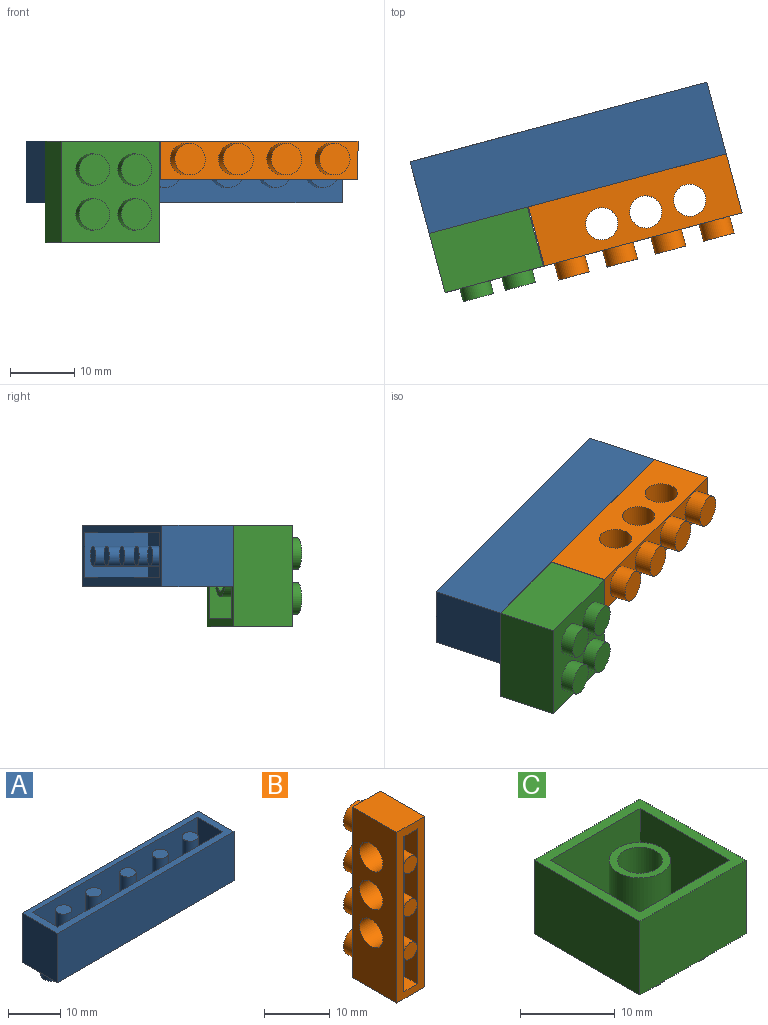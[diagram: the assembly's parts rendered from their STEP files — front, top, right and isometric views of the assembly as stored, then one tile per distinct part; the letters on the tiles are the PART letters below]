
ASSEMBLY  parts=3 mates=3
PART A: 33 faces, bbox 47.7x9.6x13.7 mm
  f0: plane 47.7x9.6mm, normal (0,0,1), area 150.9mm2, adj f1,f2,f3,f4,f18,f19,f20,f21
  f1: plane 11.5x9.6mm, normal (1,0,0), area 110.4mm2, adj f0,f2,f4,f5
  f2: plane 47.7x11.5mm, normal (0,1,0), area 548.5mm2, adj f0,f1,f3,f5
  f3: plane 11.5x9.6mm, normal (-1,0,0), area 110.4mm2, adj f0,f2,f4,f5
  f4: plane 47.7x11.5mm, normal (0,-1,0), area 548.5mm2, adj f0,f1,f3,f5
  f5: plane 47.7x9.6mm, normal (0,0,-1), area 349.3mm2, adj f1,f2,f3,f4,f6,f8,f10,f12
  f6: cylinder r=2.4mm len=4.8mm, axis (0,0,1), area 33.2mm2, adj f5,f7
  f7: plane 4.8x4.8mm, normal (0,0,-1), area 18.1mm2, adj f6
  f8: cylinder r=2.4mm len=4.8mm, axis (0,0,1), area 33.2mm2, adj f5,f9
  f9: plane 4.8x4.8mm, normal (0,0,-1), area 18.1mm2, adj f8
  f10: cylinder r=2.4mm len=4.8mm, axis (0,0,1), area 33.2mm2, adj f5,f11
  f11: plane 4.8x4.8mm, normal (0,0,-1), area 18.1mm2, adj f10
  f12: cylinder r=2.4mm len=4.8mm, axis (0,0,1), area 33.2mm2, adj f5,f13
  f13: plane 4.8x4.8mm, normal (0,0,-1), area 18.1mm2, adj f12
  f14: cylinder r=2.4mm len=4.8mm, axis (0,0,1), area 33.2mm2, adj f5,f15
  f15: plane 4.8x4.8mm, normal (0,0,-1), area 18.1mm2, adj f14
  f16: cylinder r=2.4mm len=4.8mm, axis (0,0,1), area 33.2mm2, adj f5,f17
  f17: plane 4.8x4.8mm, normal (0,0,-1), area 18.1mm2, adj f16
  f18: plane 44.54x10.15mm, normal (0,-1,0), area 452.1mm2, adj f0,f19,f21,f22
  f19: plane 10.15x6.89mm, normal (1,0,0), area 70mm2, adj f0,f18,f20,f22
  f20: plane 44.54x10.15mm, normal (0,1,0), area 452.1mm2, adj f0,f19,f21,f22
  f21: plane 10.15x6.89mm, normal (-1,0,0), area 70mm2, adj f0,f18,f20,f22
  f22: plane 44.54x6.89mm, normal (0,0,1), area 269.3mm2, adj f18,f19,f20,f21,f23,f25,f27,f29
  f23: cylinder r=1.55mm len=10.15mm, axis (0,0,-1), area 98.9mm2, adj f22,f24
  f24: plane 3.1x3.1mm, normal (0,0,1), area 7.5mm2, adj f23
  f25: cylinder r=1.55mm len=10.15mm, axis (0,0,-1), area 98.9mm2, adj f22,f26
  f26: plane 3.1x3.1mm, normal (0,0,1), area 7.5mm2, adj f25
  f27: cylinder r=1.55mm len=10.15mm, axis (0,0,-1), area 98.9mm2, adj f22,f28
  f28: plane 3.1x3.1mm, normal (0,0,1), area 7.5mm2, adj f27
  f29: cylinder r=1.55mm len=10.15mm, axis (0,0,-1), area 98.9mm2, adj f22,f30
  f30: plane 3.1x3.1mm, normal (0,0,1), area 7.5mm2, adj f29
  f31: cylinder r=1.55mm len=10.15mm, axis (0,0,-1), area 98.9mm2, adj f22,f32
  f32: plane 3.1x3.1mm, normal (0,0,1), area 7.5mm2, adj f31
PART B: 28 faces, bbox 6x12.2x31.8 mm
  f0: plane 28.9x2.78mm, normal (1,0,0), area 70.3mm2, adj f1,f6,f19,f21,f22,f23,f24,f25
  f1: plane 28.9x2.92mm, normal (0,-1,0), area 62.9mm2, adj f0,f19,f20,f21,f22,f24,f26
  f2: plane 31.77x9.5mm, normal (-1,0,0), area 242.9mm2, adj f3,f5,f6,f7,f8,f9,f10
  f3: plane 9.5x5.98mm, normal (0,0,-1), area 56.8mm2, adj f2,f4,f6,f7
  f4: plane 31.77x9.5mm, normal (1,0,0), area 242.9mm2, adj f3,f5,f6,f7,f8,f9,f10
  f5: plane 9.5x5.98mm, normal (0,0,1), area 56.8mm2, adj f2,f4,f6,f7
  f6: plane 31.77x5.98mm, normal (0,-1,0), area 105.6mm2, adj f0,f2,f3,f4,f5,f19,f20,f21
  f7: plane 31.77x5.98mm, normal (0,1,0), area 114.9mm2, adj f2,f3,f4,f5,f11,f13,f15,f17
  f8: cylinder r=2.5mm len=5.98mm, axis (1,0,0), area 93.9mm2, adj f2,f4
  f9: cylinder r=2.5mm len=5.98mm, axis (1,0,0), area 93.9mm2, adj f2,f4
  f10: cylinder r=2.5mm len=5.98mm, axis (1,0,0), area 93.9mm2, adj f2,f4
  f11: cylinder r=2.45mm len=4.89mm, axis (0,-1,0), area 41.3mm2, adj f7,f12
  f12: plane 4.89x4.89mm, normal (0,1,0), area 18.8mm2, adj f11
  f13: cylinder r=2.45mm len=4.89mm, axis (0,-1,0), area 41.3mm2, adj f7,f14
  f14: plane 4.89x4.89mm, normal (0,1,0), area 18.8mm2, adj f13
  f15: cylinder r=2.45mm len=4.89mm, axis (0,-1,0), area 41.3mm2, adj f7,f16
  f16: plane 4.89x4.89mm, normal (0,1,0), area 18.8mm2, adj f15
  f17: cylinder r=2.45mm len=4.89mm, axis (0,-1,0), area 41.3mm2, adj f7,f18
  f18: plane 4.89x4.89mm, normal (0,1,0), area 18.8mm2, adj f17
  f19: plane 2.92x2.78mm, normal (0,0,1), area 8.1mm2, adj f0,f1,f6,f20
  f20: plane 28.9x2.78mm, normal (-1,0,0), area 80.3mm2, adj f1,f6,f19,f21
  f21: plane 2.92x2.78mm, normal (0,0,-1), area 8.1mm2, adj f0,f1,f6,f20
  f22: cylinder r=1.52mm len=3.04mm, axis (0,1,0), area 22.8mm2, adj f0,f1,f23
  f23: plane 3.04x2.91mm, normal (0,-1,0), area 7.2mm2, adj f0,f22
  f24: cylinder r=1.52mm len=3.04mm, axis (0,1,0), area 22.8mm2, adj f0,f1,f25
  f25: plane 3.04x2.91mm, normal (0,-1,0), area 7.2mm2, adj f0,f24
  f26: cylinder r=1.52mm len=3.04mm, axis (0,1,0), area 22.8mm2, adj f0,f1,f27
  f27: plane 3.04x2.91mm, normal (0,-1,0), area 7.2mm2, adj f0,f26
PART C: 23 faces, bbox 15.8x15.8x11.6 mm
  f0: plane 15.8x15.8mm, normal (0,0,1), area 72.2mm2, adj f1,f2,f3,f4,f14,f15,f16,f18
  f1: plane 15.8x9.5mm, normal (1,0,0), area 150.1mm2, adj f0,f2,f4,f5
  f2: plane 15.8x9.5mm, normal (0,1,0), area 150.1mm2, adj f0,f1,f3,f5
  f3: plane 15.8x9.5mm, normal (-1,0,0), area 150.1mm2, adj f0,f2,f4,f5
  f4: plane 15.8x9.5mm, normal (0,-1,0), area 150.1mm2, adj f0,f1,f3,f5
  f5: plane 15.8x15.8mm, normal (0,0,-1), area 175.7mm2, adj f1,f2,f3,f4,f6,f8,f10,f12
  f6: cylinder r=2.43mm len=4.85mm, axis (0,0,1), area 32mm2, adj f5,f7
  f7: plane 4.85x4.85mm, normal (0,0,-1), area 18.5mm2, adj f6
  f8: cylinder r=2.43mm len=4.85mm, axis (0,0,1), area 32mm2, adj f5,f9
  f9: plane 4.85x4.85mm, normal (0,0,-1), area 18.5mm2, adj f8
  f10: cylinder r=2.43mm len=4.85mm, axis (0,0,1), area 32mm2, adj f5,f11
  f11: plane 4.85x4.85mm, normal (0,0,-1), area 18.5mm2, adj f10
  f12: cylinder r=2.43mm len=4.85mm, axis (0,0,1), area 32mm2, adj f5,f13
  f13: plane 4.85x4.85mm, normal (0,0,-1), area 18.5mm2, adj f12
  f14: plane 13.32x8.76mm, normal (-1,0,0), area 116.7mm2, adj f0,f15,f18,f19
  f15: plane 13.32x8.76mm, normal (0,-1,0), area 116.7mm2, adj f0,f14,f16,f19
  f16: plane 13.32x8.76mm, normal (1,0,0), area 116.7mm2, adj f0,f15,f18,f19
  f17: cylinder r=3.24mm len=8.76mm, axis (0,0,1), area 178.3mm2, adj f19,f20
  f18: plane 13.32x8.76mm, normal (0,1,0), area 116.7mm2, adj f0,f14,f16,f19
  f19: plane 13.32x13.32mm, normal (0,0,1), area 144.4mm2, adj f14,f15,f16,f17,f18
  f20: plane 6.48x6.48mm, normal (0,0,1), area 15.3mm2, adj f17,f21
  f21: cylinder r=2.38mm len=8.7mm, axis (0,0,1), area 129.8mm2, adj f20,f22
  f22: plane 4.75x4.75mm, normal (0,0,1), area 17.7mm2, adj f21
PLACE A rot(axis=(0.09,-0.7,-0.7),169.4deg) t=(61.23,0.09,35)mm
PLACE B rot(axis=(-0.7,-0.09,-0.7),169.4deg) t=(61.1,-9.78,58.4)mm
PLACE C rot(axis=(-0.98,-0.13,0.13),91deg) t=(48.28,-13.22,31.9)mm
MATE fastened B.f4 <-> A.f2  axis (0,0,1) through (84.27,6.26,39.8)mm
MATE fastened C.f4 <-> A.f2  axis (0,0,1) through (38.19,-6.09,39.8)mm
MATE fastened A.f23 <-> A.f29  axis (-0.26,0.97,0) through (69.84,3.79,35)mm
